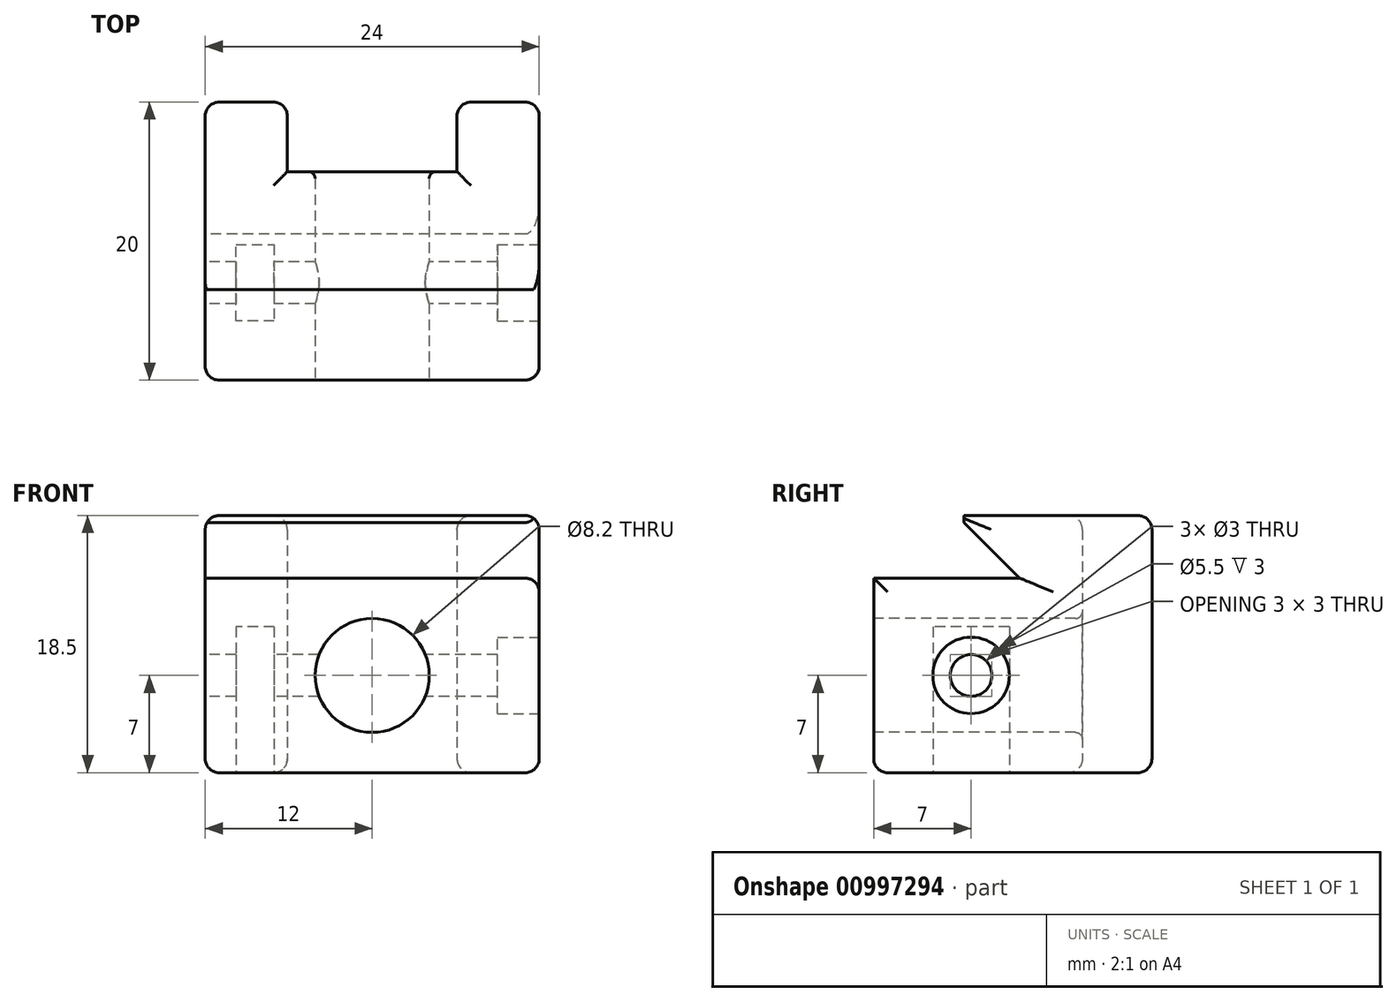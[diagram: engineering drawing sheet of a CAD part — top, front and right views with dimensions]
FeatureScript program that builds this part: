
annotation { "Feature Type Name" : "Feature", "Feature Type Description" : "" }
export const myFeature = defineFeature(function(context is Context, id is Id, definition is map)
    precondition{}
    {
        {
            var Q0;
            Q0=qCreatedBy(makeId("Top.planeOp"),FACE);
            var sketch = newSketch(context, id + "F0", { "sketchPlane" : qUnion([Q0])});
            skLineSegment(sketch, "E0.bottom", {"start": v(12, 10) * mm, "end": v(-12, 10) * mm});
            skLineSegment(sketch, "E0.top", {"start": v(12, -10) * mm, "end": v(-12, -10) * mm});
            skLineSegment(sketch, "E0.left", {"start": v(12, 10) * mm, "end": v(12, -10) * mm});
            skLineSegment(sketch, "E0.right", {"start": v(-12, 10) * mm, "end": v(-12, -10) * mm});
            skPoint(sketch, "E0.middle", {"position": v(0, 0) * mm});
            skLineSegment(sketch, "E1", {"start": v(0, 0) * mm, "end": v(0, 10) * mm, "construction": true});
            skLineSegment(sketch, "E2", {"start": v(0, 10) * mm, "end": v(6.1, 10) * mm, "construction": true});
            skLineSegment(sketch, "E3", {"start": v(6.1, 10) * mm, "end": v(6.1, 5) * mm});
            skLineSegment(sketch, "E4", {"start": v(6.1, 5) * mm, "end": v(-6.1, 5) * mm});
            skLineSegment(sketch, "E5", {"start": v(-6.1, 5) * mm, "end": v(-6.1, 10) * mm});
            skLineSegment(sketch, "E6", {"start": v(-6.1, 10) * mm, "end": v(0, 10) * mm, "construction": true});
            skSolve(sketch);
        }
        {
            var Q0;
            Q0=makeQuery(id+"F0.imprint","IMPRINT",FACE,{"disambiguationData":[TD([[makeQuery(id+"F0.imprint","IMPRINT",EDGE,{"derivedFrom":sQuery(id+"F0.wireOp",EDGE,"E0.top")}),-1.0]])]});
            extrude(context, id + "F1", {"entities" : qUnion([Q0]), "depth" : 18.5 * mm, "offsetDistance" : 25 * mm});
        }
        {
            var Q0;
            Q0=makeQuery(id+"F1.opExtrude","SWEPT_FACE",FACE,{"disambiguationData":[OSD([sQuery(id+"F0.wireOp",EDGE,"E0.right")])]});
            var sketch = newSketch(context, id + "F2", { "sketchPlane" : qUnion([Q0])});
            skLineSegment(sketch, "E7", {"start": v(-10, 18.5) * mm, "end": v(4, 18.5) * mm, "construction": true});
            skLineSegment(sketch, "E8", {"start": v(10, 0) * mm, "end": v(10, 14) * mm, "construction": true});
            skLineSegment(sketch, "E9", {"start": v(10, 14) * mm, "end": v(-0.5, 14) * mm});
            skLineSegment(sketch, "E10", {"start": v(-0.5, 14) * mm, "end": v(3.5, 18) * mm});
            skLineSegment(sketch, "E11", {"start": v(10, 0) * mm, "end": v(10, 7) * mm, "construction": true});
            skLineSegment(sketch, "E12", {"start": v(10, 7) * mm, "end": v(3, 7) * mm, "construction": true});
            skCircle(sketch, "E13", {"center": v(3, 7) * mm, "radius": 1.5 * mm});
            skLineSegment(sketch, "E14", {"start": v(4, 18.5) * mm, "end": v(3.5, 18.5) * mm, "construction": true});
            skLineSegment(sketch, "E15", {"start": v(3.5, 18.5) * mm, "end": v(3.5, 18) * mm});
            skSolve(sketch);
        }
        {
            var Q0;
            {var subQ4=sQuery(id+"F2.wireOp",EDGE,"E9");Q0=makeQuery(id+"F2.imprint","IMPRINT",FACE,{"disambiguationData":[TD([[makeQuery(id+"F2.imprint","IMPRINT",EDGE,{"derivedFrom":subQ4}),-1.0]])]});}
            var Q1;
            Q1=makeQuery(id+"F2.imprint","IMPRINT",FACE,{"disambiguationData":[TD([[makeQuery(id+"F2.imprint","IMPRINT",EDGE,{"derivedFrom":sQuery(id+"F2.wireOp",EDGE,"E13")}),1.0]])]});
            extrude(context, id + "F3", {"entities" : qUnion([Q0, Q1]), "operationType" : NewBodyOperationType.REMOVE, "oppositeDirection" : true, "depth" : 25 * mm, "offsetDistance" : 25 * mm});
        }
        {
            var Q0;
            Q0=makeQuery(id+"F1.opExtrude","SWEPT_FACE",FACE,{"disambiguationData":[OSD([sQuery(id+"F0.wireOp",EDGE,"E0.left")])]});
            var sketch = newSketch(context, id + "F4", { "sketchPlane" : qUnion([Q0])});
            skCircle(sketch, "E16", {"center": v(-3, 7) * mm, "radius": 2.75 * mm});
            skSolve(sketch);
        }
        {
            var Q0;
            Q0=makeQuery(id+"F4.imprint","IMPRINT",FACE,{"disambiguationData":[TD([[makeQuery(id+"F4.imprint","IMPRINT",EDGE,{"derivedFrom":sQuery(id+"F4.wireOp",EDGE,"E16")}),1.0]])]});
            extrude(context, id + "F5", {"entities" : qUnion([Q0]), "operationType" : NewBodyOperationType.REMOVE, "oppositeDirection" : true, "depth" : 3 * mm, "offsetDistance" : 25 * mm});
        }
        {
            var Q0;
            Q0=makeQuery(id+"F1.opExtrude","CAP_FACE",FACE,{"disambiguationData":[OSD([sQuery(id+"F0.wireOp",EDGE,"E0.bottom"),sQuery(id+"F0.wireOp",EDGE,"E0.top"),sQuery(id+"F0.wireOp",EDGE,"E0.left"),sQuery(id+"F0.wireOp",EDGE,"E0.right"),sQuery(id+"F0.wireOp",EDGE,"E3"),sQuery(id+"F0.wireOp",EDGE,"E4"),sQuery(id+"F0.wireOp",EDGE,"E5")])],"isStart":true});
            var sketch = newSketch(context, id + "F6", { "sketchPlane" : qUnion([Q0])});
            skLineSegment(sketch, "E17", {"start": v(0, 10) * mm, "end": v(0, 3) * mm, "construction": true});
            skLineSegment(sketch, "E18", {"start": v(0, 3) * mm, "end": v(-7.05, 3) * mm, "construction": true});
            skLineSegment(sketch, "E19", {"start": v(-7.05, 3) * mm, "end": v(-7.05, 5.75) * mm});
            skLineSegment(sketch, "E20", {"start": v(-7.05, 5.75) * mm, "end": v(-9.8, 5.75) * mm});
            skLineSegment(sketch, "E21", {"start": v(-9.8, 5.75) * mm, "end": v(-9.8, 0.25) * mm});
            skLineSegment(sketch, "E22", {"start": v(-9.8, 0.25) * mm, "end": v(-7.05, 0.25) * mm});
            skLineSegment(sketch, "E23", {"start": v(-7.05, 0.25) * mm, "end": v(-7.05, 3) * mm});
            skSolve(sketch);
        }
        {
            var Q0;
            Q0=makeQuery(id+"F6.imprint","IMPRINT",FACE,{"disambiguationData":[TD([[makeQuery(id+"F6.imprint","IMPRINT",EDGE,{"derivedFrom":sQuery(id+"F6.wireOp",EDGE,"E19")}),1.0]])]});
            extrude(context, id + "F7", {"entities" : qUnion([Q0]), "operationType" : NewBodyOperationType.REMOVE, "oppositeDirection" : true, "depth" : 10.5 * mm, "offsetDistance" : 25 * mm});
        }
        {
            var Q0;
            Q0=makeQuery(id+"F1.opExtrude","SWEPT_FACE",FACE,{"disambiguationData":[OSD([sQuery(id+"F0.wireOp",EDGE,"E0.top")])]});
            var sketch = newSketch(context, id + "F8", { "sketchPlane" : qUnion([Q0])});
            skLineSegment(sketch, "E24", {"start": v(0, 0) * mm, "end": v(0, 14) * mm, "construction": true});
            skCircle(sketch, "E25", {"center": v(0, 7) * mm, "radius": 4.1 * mm});
            skSolve(sketch);
        }
        {
            var Q0;
            Q0=makeQuery(id+"F8.imprint","IMPRINT",FACE,{"disambiguationData":[TD([[makeQuery(id+"F8.imprint","IMPRINT",EDGE,{"derivedFrom":sQuery(id+"F8.wireOp",EDGE,"E25")}),1.0]])]});
            extrude(context, id + "F9", {"entities" : qUnion([Q0]), "operationType" : NewBodyOperationType.REMOVE, "oppositeDirection" : true, "depth" : 25 * mm, "offsetDistance" : 25 * mm});
        }
        {
            var Q0;
            Q0=makeQuery(id+"F3.boolean.opBoolean","INTERSECT",EDGE,{"derivedFrom":[makeQuery(id+"F1.opExtrude","SWEPT_FACE",FACE,{"disambiguationData":[OSD([sQuery(id+"F0.wireOp",EDGE,"E0.left")])]}),makeQuery(id+"F3.opExtrude","SWEPT_FACE",FACE,{"disambiguationData":[OSD([sQuery(id+"F2.wireOp",EDGE,"E9")])]})]});
            var Q1;
            Q1=makeQuery(id+"F3.boolean.opBoolean","INTERSECT",EDGE,{"derivedFrom":[makeQuery(id+"F1.opExtrude","SWEPT_FACE",FACE,{"disambiguationData":[OSD([sQuery(id+"F0.wireOp",EDGE,"E0.left")])]}),makeQuery(id+"F3.opExtrude","SWEPT_FACE",FACE,{"disambiguationData":[OSD([sQuery(id+"F2.wireOp",EDGE,"E10")])]})]});
            var Q2;
            Q2=makeQuery(id+"F1.opExtrude","CAP_EDGE",EDGE,{"disambiguationData":[OSD([sQuery(id+"F0.wireOp",EDGE,"E0.left")])],"isStart":false});
            var Q3;
            Q3=makeQuery(id+"F1.opExtrude","SWEPT_EDGE",EDGE,{"disambiguationData":[OSD([sQuery(id+"F0.wireOp",EDGE,"E0.bottom"),sQuery(id+"F0.wireOp",EDGE,"E0.left")])]});
            var Q4;
            Q4=makeQuery(id+"F1.opExtrude","SWEPT_EDGE",EDGE,{"disambiguationData":[OSD([sQuery(id+"F0.wireOp",EDGE,"E0.top"),sQuery(id+"F0.wireOp",EDGE,"E0.left")])]});
            var Q5;
            Q5=makeQuery(id+"F1.opExtrude","CAP_EDGE",EDGE,{"disambiguationData":[OSD([sQuery(id+"F0.wireOp",EDGE,"E0.left")])],"isStart":true});
            var Q6;
            {var subQ0=sQuery(id+"F0.wireOp",EDGE,"E0.bottom");Q6=makeQuery(id+"F1.opExtrude","CAP_EDGE",EDGE,{"disambiguationData":[OSD([subQ0]),TDD([makeQuery(id+"F0.imprint","IMPRINT",EDGE,{"disambiguationData":[TD([[makeQuery(id+"F0.imprint","INTERSECT",VERTEX,{"derivedFrom":[subQ0,sQuery(id+"F0.wireOp",EDGE,"E0.left")]}),-1.0]])],"derivedFrom":subQ0})])],"isStart":false});}
            var Q7;
            Q7=makeQuery(id+"F1.opExtrude","CAP_EDGE",EDGE,{"disambiguationData":[OSD([sQuery(id+"F0.wireOp",EDGE,"E3")])],"isStart":false});
            var Q8;
            Q8=makeQuery(id+"F1.opExtrude","CAP_EDGE",EDGE,{"disambiguationData":[OSD([sQuery(id+"F0.wireOp",EDGE,"E4")])],"isStart":false});
            var Q9;
            Q9=makeQuery(id+"F1.opExtrude","CAP_EDGE",EDGE,{"disambiguationData":[OSD([sQuery(id+"F0.wireOp",EDGE,"E5")])],"isStart":false});
            var Q10;
            {var subQ0=sQuery(id+"F0.wireOp",EDGE,"E0.bottom");Q10=makeQuery(id+"F1.opExtrude","CAP_EDGE",EDGE,{"disambiguationData":[OSD([subQ0]),TDD([makeQuery(id+"F0.imprint","IMPRINT",EDGE,{"disambiguationData":[TD([[makeQuery(id+"F0.imprint","INTERSECT",VERTEX,{"derivedFrom":[subQ0,sQuery(id+"F0.wireOp",EDGE,"E0.right")]}),1.0]])],"derivedFrom":subQ0})])],"isStart":false});}
            var Q11;
            Q11=makeQuery(id+"F1.opExtrude","SWEPT_EDGE",EDGE,{"disambiguationData":[OSD([sQuery(id+"F0.wireOp",EDGE,"E0.bottom"),sQuery(id+"F0.wireOp",EDGE,"E5")])]});
            var Q12;
            Q12=makeQuery(id+"F1.opExtrude","SWEPT_EDGE",EDGE,{"disambiguationData":[OSD([sQuery(id+"F0.wireOp",EDGE,"E0.bottom"),sQuery(id+"F0.wireOp",EDGE,"E3")])]});
            var Q13;
            {var subQ0=sQuery(id+"F0.wireOp",EDGE,"E0.bottom");Q13=makeQuery(id+"F1.opExtrude","CAP_EDGE",EDGE,{"disambiguationData":[OSD([subQ0]),TDD([makeQuery(id+"F0.imprint","IMPRINT",EDGE,{"disambiguationData":[TD([[makeQuery(id+"F0.imprint","INTERSECT",VERTEX,{"derivedFrom":[subQ0,sQuery(id+"F0.wireOp",EDGE,"E0.left")]}),-1.0]])],"derivedFrom":subQ0})])],"isStart":true});}
            var Q14;
            Q14=makeQuery(id+"F1.opExtrude","CAP_EDGE",EDGE,{"disambiguationData":[OSD([sQuery(id+"F0.wireOp",EDGE,"E3")])],"isStart":true});
            var Q15;
            Q15=makeQuery(id+"F1.opExtrude","CAP_EDGE",EDGE,{"disambiguationData":[OSD([sQuery(id+"F0.wireOp",EDGE,"E5")])],"isStart":true});
            var Q16;
            Q16=makeQuery(id+"F1.opExtrude","SWEPT_EDGE",EDGE,{"disambiguationData":[OSD([sQuery(id+"F0.wireOp",EDGE,"E0.bottom"),sQuery(id+"F0.wireOp",EDGE,"E0.right")])]});
            var Q17;
            {var subQ0=sQuery(id+"F0.wireOp",EDGE,"E0.bottom");Q17=makeQuery(id+"F1.opExtrude","CAP_EDGE",EDGE,{"disambiguationData":[OSD([subQ0]),TDD([makeQuery(id+"F0.imprint","IMPRINT",EDGE,{"disambiguationData":[TD([[makeQuery(id+"F0.imprint","INTERSECT",VERTEX,{"derivedFrom":[subQ0,sQuery(id+"F0.wireOp",EDGE,"E0.right")]}),1.0]])],"derivedFrom":subQ0})])],"isStart":true});}
            var Q18;
            Q18=makeQuery(id+"F1.opExtrude","CAP_EDGE",EDGE,{"disambiguationData":[OSD([sQuery(id+"F0.wireOp",EDGE,"E0.right")])],"isStart":true});
            var Q19;
            Q19=makeQuery(id+"F1.opExtrude","CAP_EDGE",EDGE,{"disambiguationData":[OSD([sQuery(id+"F0.wireOp",EDGE,"E0.top")])],"isStart":true});
            var Q20;
            Q20=makeQuery(id+"F7.boolean.opBoolean","COPY",EDGE,{"derivedFrom":makeQuery(id+"F7.opExtrude","CAP_EDGE",EDGE,{"disambiguationData":[OSD([sQuery(id+"F6.wireOp",EDGE,"E20")])],"isStart":true})});
            var Q21;
            Q21=makeQuery(id+"F7.boolean.opBoolean","COPY",EDGE,{"derivedFrom":makeQuery(id+"F7.opExtrude","CAP_EDGE",EDGE,{"disambiguationData":[OSD([sQuery(id+"F6.wireOp",EDGE,"E19"),sQuery(id+"F6.wireOp",EDGE,"E23")])],"isStart":true})});
            var Q22;
            Q22=makeQuery(id+"F7.boolean.opBoolean","COPY",EDGE,{"derivedFrom":makeQuery(id+"F7.opExtrude","CAP_EDGE",EDGE,{"disambiguationData":[OSD([sQuery(id+"F6.wireOp",EDGE,"E21")])],"isStart":true})});
            var Q23;
            Q23=makeQuery(id+"F7.boolean.opBoolean","COPY",EDGE,{"derivedFrom":makeQuery(id+"F7.opExtrude","CAP_EDGE",EDGE,{"disambiguationData":[OSD([sQuery(id+"F6.wireOp",EDGE,"E22")])],"isStart":true})});
            var Q24;
            Q24=makeQuery(id+"F1.opExtrude","CAP_EDGE",EDGE,{"disambiguationData":[OSD([sQuery(id+"F0.wireOp",EDGE,"E4")])],"isStart":true});
            var Q25;
            Q25=makeQuery(id+"F3.boolean.opBoolean","COPY",EDGE,{"derivedFrom":makeQuery(id+"F3.opExtrude","CAP_EDGE",EDGE,{"disambiguationData":[OSD([sQuery(id+"F2.wireOp",EDGE,"E9")])],"isStart":true})});
            var Q26;
            Q26=makeQuery(id+"F3.boolean.opBoolean","COPY",EDGE,{"derivedFrom":makeQuery(id+"F3.opExtrude","SWEPT_EDGE",EDGE,{"disambiguationData":[OSD([sQuery(id+"F0.wireOp",EDGE,"E0.top"),sQuery(id+"F0.wireOp",EDGE,"E0.right"),sQuery(id+"F2.wireOp",EDGE,"E9")])]})});
            var Q27;
            Q27=makeQuery(id+"F1.opExtrude","SWEPT_EDGE",EDGE,{"disambiguationData":[OSD([sQuery(id+"F0.wireOp",EDGE,"E0.top"),sQuery(id+"F0.wireOp",EDGE,"E0.right")])]});
            var Q28;
            Q28=makeQuery(id+"F1.opExtrude","CAP_EDGE",EDGE,{"disambiguationData":[OSD([sQuery(id+"F0.wireOp",EDGE,"E0.right")])],"isStart":false});
            var Q29;
            Q29=makeQuery(id+"F3.boolean.opBoolean","COPY",EDGE,{"derivedFrom":makeQuery(id+"F3.opExtrude","CAP_EDGE",EDGE,{"disambiguationData":[OSD([sQuery(id+"F2.wireOp",EDGE,"E10")])],"isStart":true})});
            fillet(context, id + "F10", {"entities" : qUnion([Q0, Q1, Q2, Q3, Q4, Q5, Q6, Q7, Q8, Q9, Q10, Q11, Q12, Q13, Q14, Q15, Q16, Q17, Q18, Q19, Q20, Q21, Q22, Q23, Q24, Q25, Q26, Q27, Q28, Q29]), "radius" : 1 * mm, "tangentPropagation" : true, "allowEdgeOverflow" : false});
        }
        {
            var Q0;
            Q0=makeQuery(id+"F9.boolean.opBoolean","INTERSECT",EDGE,{"derivedFrom":[makeQuery(id+"F1.opExtrude","SWEPT_FACE",FACE,{"disambiguationData":[OSD([sQuery(id+"F0.wireOp",EDGE,"E4")])]}),makeQuery(id+"F9.opExtrude","SWEPT_FACE",FACE,{"disambiguationData":[OSD([sQuery(id+"F8.wireOp",EDGE,"E25")])]})]});
            var Q1;
            Q1=makeQuery(id+"F9.boolean.opBoolean","COPY",EDGE,{"derivedFrom":makeQuery(id+"F9.opExtrude","CAP_EDGE",EDGE,{"disambiguationData":[OSD([sQuery(id+"F8.wireOp",EDGE,"E25")])],"isStart":true})});
            var Q2;
            Q2=makeQuery(id+"F5.boolean.opBoolean","COPY",EDGE,{"derivedFrom":makeQuery(id+"F5.opExtrude","CAP_EDGE",EDGE,{"disambiguationData":[OSD([sQuery(id+"F4.wireOp",EDGE,"E16")])],"isStart":true})});
            var Q3;
            Q3=makeQuery(id+"F5.boolean.opBoolean","COPY",EDGE,{"derivedFrom":makeQuery(id+"F5.opExtrude","CAP_EDGE",EDGE,{"disambiguationData":[OSD([sQuery(id+"F0.wireOp",EDGE,"E0.left"),sQuery(id+"F2.wireOp",EDGE,"E13")])],"isStart":false})});
            var Q4;
            Q4=makeQuery(id+"F3.boolean.opBoolean","COPY",EDGE,{"derivedFrom":makeQuery(id+"F3.opExtrude","CAP_EDGE",EDGE,{"disambiguationData":[OSD([sQuery(id+"F2.wireOp",EDGE,"E13")])],"isStart":true})});
            fillet(context, id + "F11", {"entities" : qUnion([Q0, Q1, Q2, Q3, Q4]), "radius" : .5 * mm, "tangentPropagation" : true, "allowEdgeOverflow" : false});
        }
    });
